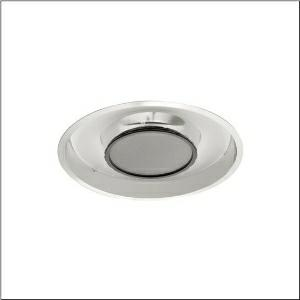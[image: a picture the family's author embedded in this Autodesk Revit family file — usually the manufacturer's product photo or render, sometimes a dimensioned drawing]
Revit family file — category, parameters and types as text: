
# Revit family: lunis_11_r_5lr610d4ob11af
name_source: partatom
category: Lighting Fixtures
units: mm (PartAtom-declared; Revit-internal decimal feet)

## family parameters
Cut with Voids When Loaded = No
Host = Face
Light Source = No
Part Type = Normal
Room Calculation Point = No
Round Connector Dimension = Use Diameter
Shared = No

## types (1)
- --- (1 x LED 4000K / CRI = 80 (unbekannt), 4860 lm, 4000K)
    Apparent Load = 37 VA
    CIE Flux Codes = 60 90 99 100 100
    Color Rendering = 80
    Color Temperature = 4000K
    Default Elevation = 1800 mm
    Description = Lunis 11 R, downlight, light control with reflector, of ultra-pure aluminium (Al 99.98%), highly specular, perforated, light emission: direct distribution, LED rated luminous flux: 4.860lm, light colour: 840, control gear: ECG Multilumen, with terminal, 3+2-pole, max. 2.5mm², mains connection: 230V, AC, 50/60Hz, diameter: 398mm, central ring, of plastic, graphite (RAL 7037), central module, blanking cover, of sheet steel, perforated, metallic grey (RAL 9006), protection rating (complete): IP20, insulation class (complete): insulation class II (safety insulation), certification: CE, ENEC, VDE, protection symbol: F, permissible ambient temperature for indoor applications: +10..+35°C, standard: EN 50419, packaging unit: 1 piece
    Height = 0 mm  [stored 0 ft]
    Lamp = 1 x LED 4000K / CRI >= 80 (unbekannt)
    Lamp Light Flux = 4860 lm
    Lamp count = 1
    Length = 398 mm
    Luminous efficacy = 131 lm/W
    Manufacturer = Siteco
    ModVariant = No
    Model = 5LR610D4OB11AF
    Mounting Place = Ceiling
    Mounting Type = Recessed
    Number of Poles = 1
    OnlyDefault = Yes
    Power Factor = 1
    Product Name = Lunis 11 R
    Product group = downlight
    ProductGroupID = 401
    Protection Class = Protection class II
    Protection Degree = IP 20
    RLX_Detail_Level = 1
    RLX_Emergency_Light_Flux = 0 lm
    RLX_Emergency_Type = 0
    RLX_Emergency_Type_DB = No
    RlxData = <blob elided: 94457 chars, md5=7984cd5c>
    Socket = socket
    Standby Power = 0 W
    System Light Flux = 4860 lm
    System Power = 37 W
    Type Comments = factory setting: High Lumen Output
    Type Image = l_1003323.jpg
    URL = http://relux.com
    VarID = @adj_219821
    Voltage = 0 V
    Weight = 0.00 kg
    Width = 0 mm  [stored 0 ft]

note: [stored X ft] marks values corroborated as IEEE doubles in the binary element streams (Revit-internal decimal feet)

## geometry (parser evidence)
native form markers: Blend x4, Sweep x10
no freeform markers — native parametric forms only
